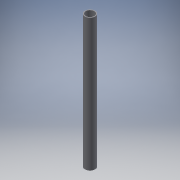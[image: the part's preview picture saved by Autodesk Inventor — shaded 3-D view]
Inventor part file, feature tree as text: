
AUTODESK INVENTOR PART (.ipt)
format: ipt  version: 2017 (Build 210142000, 142)  size: 91,136 bytes
history: native  units: in
note: dims shown in document units (in); Inventor stores cm internally (conversion verified against a paired STEP export)
features: extrude x1, sketch x1
ambient origin geometry x8: Origin, YZ Plane, XZ Plane, XY Plane, X Axis, Y Axis, Z Axis, Center Point
bodies: Solid1 (feature_tree)
feature tree (2):
  extrude  "Extrusion1"  Depth=7.0in
  sketch  "Sketch1"  dims[d0=0.45in d1=0.54in d2=7.0in d3=0.0in]
